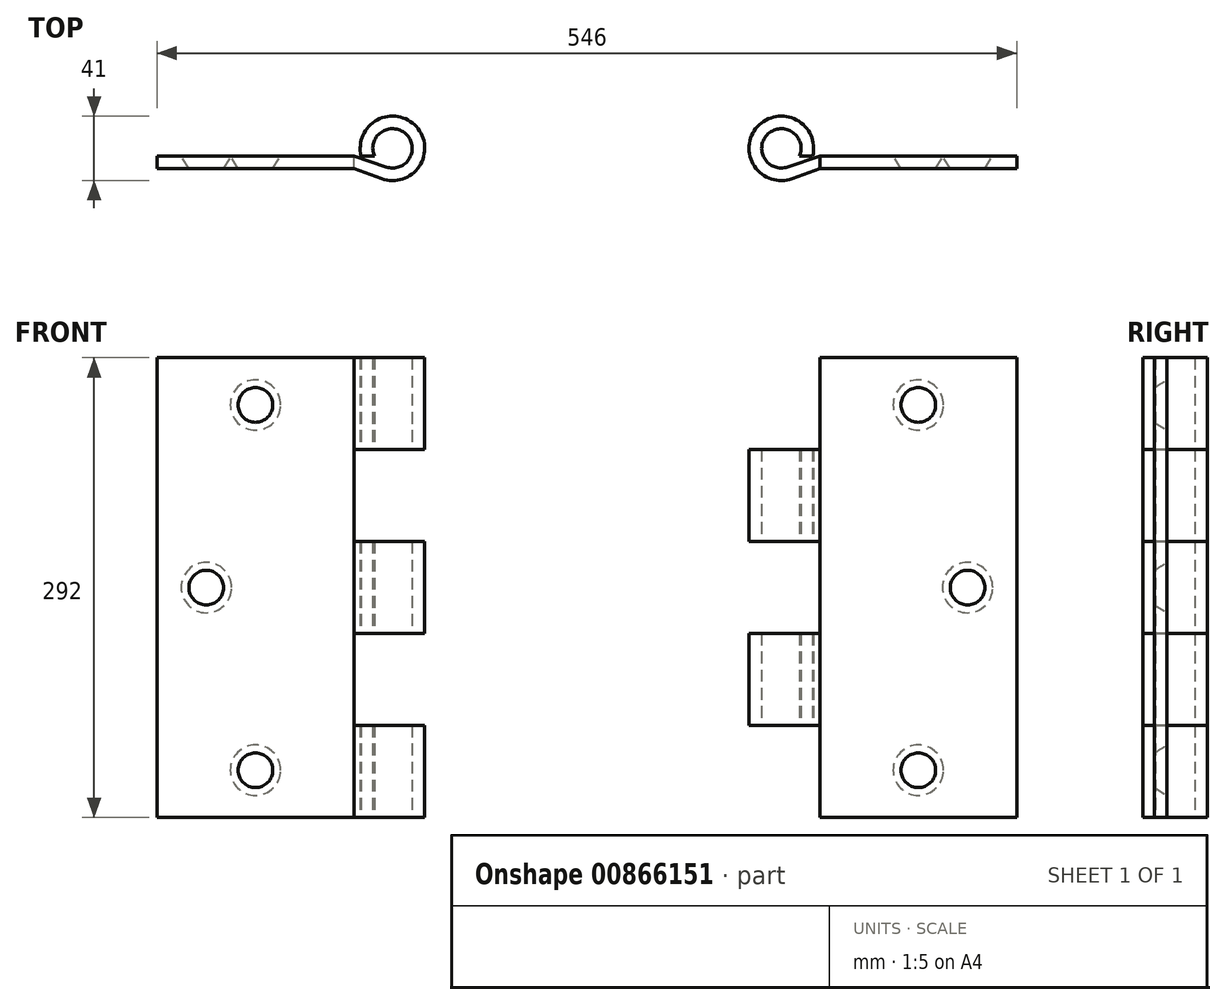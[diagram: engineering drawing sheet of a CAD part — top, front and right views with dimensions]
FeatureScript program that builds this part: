
annotation { "Feature Type Name" : "Feature", "Feature Type Description" : "" }
export const myFeature = defineFeature(function(context is Context, id is Id, definition is map)
    precondition{}
    {
        {
            var Q0;
            Q0=qCreatedBy(makeId("Top.planeOp"),FACE);
            var sketch = newSketch(context, id + "F0", { "sketchPlane" : qUnion([Q0])});
            skLineSegment(sketch, "E0", {"start": v(0, 0) * mm, "end": v(-125, 0) * mm});
            skLineSegment(sketch, "E1", {"start": v(-125, 0) * mm, "end": v(-125, 8) * mm});
            skLineSegment(sketch, "E2", {"start": v(0, 0) * mm, "end": v(0, 0) * mm});
            skLineSegment(sketch, "E3", {"start": v(-125, 8) * mm, "end": v(0, 8) * mm});
            skLineSegment(sketch, "E4", {"start": v(0, 8) * mm, "end": v(0, 13) * mm});
            skArc(sketch, "E5", {"start": v(20.54, 1.14) * mm, "mid": v(32.94, 22.22) * mm, "end": v(13.04, 8) * mm});
            skArc(sketch, "E6", {"start": v(17.59, -6.3) * mm, "mid": v(39.69, 26.77) * mm, "end": v(4.62, 8) * mm});
            skLineSegment(sketch, "E7", {"start": v(0, 0) * mm, "end": v(17.59, -6.3) * mm});
            skLineSegment(sketch, "E8", {"start": v(0, 8) * mm, "end": v(20.54, 1.14) * mm});
            skLineSegment(sketch, "E9", {"start": v(4.62, 8) * mm, "end": v(13.04, 8) * mm});
            skSolve(sketch);
        }
        {
            var Q0;
            Q0=makeQuery(id+"F0.imprint","IMPRINT",FACE,{"disambiguationData":[TD([[makeQuery(id+"F0.imprint","IMPRINT",EDGE,{"derivedFrom":sQuery(id+"F0.wireOp",EDGE,"E0")}),-1.0]])]});
            extrude(context, id + "F1", {"entities" : qUnion([Q0]), "depth" : 292 * mm, "offsetDistance" : 25 * mm});
        }
        {
            var Q0;
            Q0=makeQuery(id+"F1.opExtrude","SWEPT_FACE",FACE,{"disambiguationData":[OSD([sQuery(id+"F0.wireOp",EDGE,"E3")])]});
            var sketch = newSketch(context, id + "F2", { "sketchPlane" : qUnion([Q0])});
            skLineSegment(sketch, "E10", {"start": v(125, 292) * mm, "end": v(125, 262) * mm});
            skLineSegment(sketch, "E11", {"start": v(125, 292) * mm, "end": v(125, 146) * mm});
            skCircle(sketch, "E12", {"center": v(62.5, 262) * mm, "radius": 16 * mm});
            skPoint(sketch, "E12.centerSnap0", {"position": v(62.5, 292) * mm});
            skCircle(sketch, "E13", {"center": v(93.75, 146) * mm, "radius": 16 * mm});
            skPoint(sketch, "E13.centerSnap0", {"position": v(93.75, 292) * mm});
            skCircle(sketch, "E14", {"center": v(62.5, 30) * mm, "radius": 16 * mm});
            skPoint(sketch, "E15.start.orphan", {"position": v(62.5, 0) * mm});
            skSolve(sketch);
        }
        {
            var Q0;
            Q0=makeQuery(id+"F1.opExtrude","SWEPT_FACE",FACE,{"disambiguationData":[OSD([sQuery(id+"F0.wireOp",EDGE,"E0")])]});
            var sketch = newSketch(context, id + "F3", { "sketchPlane" : qUnion([Q0])});
            skPoint(sketch, "E16.0", {"position": v(-93.75, 146) * mm});
            skPoint(sketch, "E16.1", {"position": v(-62.5, 262) * mm});
            skPoint(sketch, "E16.2", {"position": v(-62.5, 30) * mm});
            skCircle(sketch, "E17", {"center": v(-62.5, 30) * mm, "radius": 11 * mm});
            skCircle(sketch, "E18", {"center": v(-93.75, 146) * mm, "radius": 11 * mm});
            skCircle(sketch, "E19", {"center": v(-62.5, 262) * mm, "radius": 11 * mm});
            skSolve(sketch);
        }
        {
            var Q1;
            Q1=makeQuery(id+"F2.imprint","IMPRINT",FACE,{"disambiguationData":[TD([[makeQuery(id+"F2.imprint","IMPRINT",EDGE,{"derivedFrom":sQuery(id+"F2.wireOp",EDGE,"E14")}),1.0]])]});
            var Q2;
            Q2=makeQuery(id+"F3.imprint","IMPRINT",FACE,{"disambiguationData":[TD([[makeQuery(id+"F3.imprint","IMPRINT",EDGE,{"derivedFrom":sQuery(id+"F3.wireOp",EDGE,"E17")}),1.0]])]});
            loft(context, id + "F4", {"operationType" : NewBodyOperationType.REMOVE, "sheetProfilesArray" : [{ "sheetProfileEntities" : qUnion([Q1]) }, { "sheetProfileEntities" : qUnion([Q2]) }]});
        }
        {
            var Q1;
            Q1=makeQuery(id+"F2.imprint","IMPRINT",FACE,{"disambiguationData":[TD([[makeQuery(id+"F2.imprint","IMPRINT",EDGE,{"derivedFrom":sQuery(id+"F2.wireOp",EDGE,"E13")}),1.0]])]});
            var Q2;
            Q2=makeQuery(id+"F3.imprint","IMPRINT",FACE,{"disambiguationData":[TD([[makeQuery(id+"F3.imprint","IMPRINT",EDGE,{"derivedFrom":sQuery(id+"F3.wireOp",EDGE,"E18")}),1.0]])]});
            loft(context, id + "F5", {"operationType" : NewBodyOperationType.REMOVE, "sheetProfilesArray" : [{ "sheetProfileEntities" : qUnion([Q1]) }, { "sheetProfileEntities" : qUnion([Q2]) }]});
        }
        {
            var Q1;
            Q1=makeQuery(id+"F2.imprint","IMPRINT",FACE,{"disambiguationData":[TD([[makeQuery(id+"F2.imprint","IMPRINT",EDGE,{"derivedFrom":sQuery(id+"F2.wireOp",EDGE,"E12")}),1.0]])]});
            var Q2;
            Q2=makeQuery(id+"F3.imprint","IMPRINT",FACE,{"disambiguationData":[TD([[makeQuery(id+"F3.imprint","IMPRINT",EDGE,{"derivedFrom":sQuery(id+"F3.wireOp",EDGE,"E19")}),1.0]])]});
            loft(context, id + "F6", {"operationType" : NewBodyOperationType.REMOVE, "sheetProfilesArray" : [{ "sheetProfileEntities" : qUnion([Q1]) }, { "sheetProfileEntities" : qUnion([Q2]) }]});
        }
        {
            var Q0;
            Q0=qCreatedBy(makeId("Right.planeOp"),FACE);
            cPlane(context, id + "F7", {"entities" : qUnion([Q0]), "cplaneType" : CPlaneType.OFFSET, "offset" : 148 * mm, "width" : 150 * mm, "height" : 150 * mm});
        }
        {
            var Q0;
            Q0=makeQuery(id+"F1.opExtrude","SWEPT_BODY",BODY,{"disambiguationData":[OSD([sQuery(id+"F0.wireOp",EDGE,"E0"),sQuery(id+"F0.wireOp",EDGE,"E1"),sQuery(id+"F0.wireOp",EDGE,"E3"),sQuery(id+"F0.wireOp",EDGE,"E5"),sQuery(id+"F0.wireOp",EDGE,"E6"),sQuery(id+"F0.wireOp",EDGE,"E7"),sQuery(id+"F0.wireOp",EDGE,"E8"),sQuery(id+"F0.wireOp",EDGE,"E9")])]});
            var Q1;
            Q1=qCreatedBy(id+"F7.planeOp",FACE);
            mirror(context, id + "F8", {"entities" : qUnion([Q0]), "mirrorPlane" : qUnion([Q1])});
        }
        {
            var Q0;
            Q0=makeQuery(id+"F2.imprint","IMPRINT",FACE,{"disambiguationData":[TD([[makeQuery(id+"F2.imprint","IMPRINT",EDGE,{"derivedFrom":sQuery(id+"F2.wireOp",EDGE,"E12")}),-1.0]])]});
            var sketch = newSketch(context, id + "F9", { "sketchPlane" : qUnion([Q0])});
            skLineSegment(sketch, "E20", {"start": v(0, 0) * mm, "end": v(0, 58.4) * mm});
            skLineSegment(sketch, "E21", {"start": v(0, 58.4) * mm, "end": v(-56.85, 58.4) * mm});
            skLineSegment(sketch, "E22", {"start": v(-56.85, 58.4) * mm, "end": v(-56.85, 0) * mm});
            skLineSegment(sketch, "E23", {"start": v(-56.85, 0) * mm, "end": v(0, 0) * mm});
            skLineSegment(sketch, "E24", {"start": v(0, 58.4) * mm, "end": v(0, 116.8) * mm});
            skLineSegment(sketch, "E25", {"start": v(0, 116.8) * mm, "end": v(-63.77, 116.8) * mm});
            skLineSegment(sketch, "E26", {"start": v(-63.77, 116.8) * mm, "end": v(-63.77, 58.4) * mm});
            skLineSegment(sketch, "E27", {"start": v(-63.77, 58.4) * mm, "end": v(-56.85, 58.4) * mm});
            skLineSegment(sketch, "E28", {"start": v(0, 116.8) * mm, "end": v(0, 175.2) * mm});
            skLineSegment(sketch, "E29", {"start": v(0, 175.2) * mm, "end": v(-56.85, 175.2) * mm});
            skLineSegment(sketch, "E30", {"start": v(-56.85, 175.2) * mm, "end": v(-56.85, 116.8) * mm});
            skLineSegment(sketch, "E31", {"start": v(0, 175.2) * mm, "end": v(0, 233.6) * mm});
            skLineSegment(sketch, "E32", {"start": v(0, 233.6) * mm, "end": v(-57.4, 233.6) * mm});
            skLineSegment(sketch, "E33", {"start": v(-57.4, 233.6) * mm, "end": v(-57.4, 175.2) * mm});
            skLineSegment(sketch, "E34", {"start": v(-57.4, 175.2) * mm, "end": v(-56.85, 175.2) * mm});
            skLineSegment(sketch, "E35", {"start": v(0, 233.6) * mm, "end": v(0, 292) * mm});
            skLineSegment(sketch, "E36", {"start": v(0, 292) * mm, "end": v(-69.69, 292) * mm});
            skLineSegment(sketch, "E37", {"start": v(-69.69, 292) * mm, "end": v(-69.69, 233.6) * mm});
            skLineSegment(sketch, "E38", {"start": v(-69.69, 233.6) * mm, "end": v(-57.4, 233.6) * mm});
            skSolve(sketch);
        }
        {
            var Q0;
            Q0=makeQuery(id+"F9.imprint","IMPRINT",FACE,{"disambiguationData":[TD([[makeQuery(id+"F9.imprint","IMPRINT",EDGE,{"derivedFrom":sQuery(id+"F9.wireOp",EDGE,"E29")}),-1.0]])]});
            var Q1;
            Q1=makeQuery(id+"F9.imprint","IMPRINT",FACE,{"disambiguationData":[TD([[makeQuery(id+"F9.imprint","IMPRINT",EDGE,{"derivedFrom":sQuery(id+"F9.wireOp",EDGE,"E21")}),-1.0]])]});
            extrude(context, id + "F10", {"entities" : qUnion([Q0, Q1]), "operationType" : NewBodyOperationType.REMOVE, "endBound" : BoundingType.SYMMETRIC, "oppositeDirection" : true, "depth" : 100 * mm, "offsetDistance" : 25 * mm});
        }
        {
            var Q0;
            Q0=makeQuery(id+"F8.opPattern","COPY",FACE,{"derivedFrom":makeQuery(id+"F1.opExtrude","SWEPT_FACE",FACE,{"disambiguationData":[OSD([sQuery(id+"F0.wireOp",EDGE,"E3")])]}),"instanceName":"1"});
            var sketch = newSketch(context, id + "F11", { "sketchPlane" : qUnion([Q0])});
            skLineSegment(sketch, "E39", {"start": v(-296, 292) * mm, "end": v(-296, 233.6) * mm});
            skLineSegment(sketch, "E40", {"start": v(-296, 233.6) * mm, "end": v(-237.8, 233.6) * mm});
            skLineSegment(sketch, "E41", {"start": v(-237.8, 233.6) * mm, "end": v(-237.8, 175.2) * mm});
            skLineSegment(sketch, "E42", {"start": v(-237.8, 175.2) * mm, "end": v(-296, 175.2) * mm});
            skLineSegment(sketch, "E43", {"start": v(-296, 175.2) * mm, "end": v(-296, 116.8) * mm});
            skLineSegment(sketch, "E44", {"start": v(-296, 116.8) * mm, "end": v(-240.26, 116.8) * mm});
            skLineSegment(sketch, "E45", {"start": v(-240.26, 116.8) * mm, "end": v(-240.26, 58.4) * mm});
            skLineSegment(sketch, "E46", {"start": v(-240.26, 58.4) * mm, "end": v(-296, 58.4) * mm});
            skLineSegment(sketch, "E47", {"start": v(-296, 58.4) * mm, "end": v(-296, 0) * mm});
            skLineSegment(sketch, "E48", {"start": v(-296, 0) * mm, "end": v(-240.3, 0) * mm});
            skLineSegment(sketch, "E49", {"start": v(-240.3, 0) * mm, "end": v(-234.18, 0) * mm});
            skLineSegment(sketch, "E50", {"start": v(-234.18, 0) * mm, "end": v(-234.18, 58.4) * mm});
            skLineSegment(sketch, "E51", {"start": v(-234.18, 58.4) * mm, "end": v(-240.26, 58.4) * mm});
            skLineSegment(sketch, "E52", {"start": v(-296, 58.4) * mm, "end": v(-296, 116.8) * mm});
            skLineSegment(sketch, "E53", {"start": v(-240.26, 116.8) * mm, "end": v(-240.26, 175.2) * mm});
            skLineSegment(sketch, "E54", {"start": v(-237.8, 233.6) * mm, "end": v(-237.8, 292) * mm});
            skLineSegment(sketch, "E55", {"start": v(-237.8, 292) * mm, "end": v(-296, 292) * mm});
            skSolve(sketch);
        }
        {
            var Q0;
            Q0=makeQuery(id+"F11.imprint","IMPRINT",FACE,{"disambiguationData":[TD([[makeQuery(id+"F11.imprint","IMPRINT",EDGE,{"derivedFrom":sQuery(id+"F11.wireOp",EDGE,"E39")}),1.0]])]});
            var Q1;
            {var subQ0=sQuery(id+"F11.wireOp",EDGE,"E43");Q1=makeQuery(id+"F11.imprint","IMPRINT",FACE,{"disambiguationData":[TD([[makeQuery(id+"F11.imprint","IMPRINT",EDGE,{"derivedFrom":subQ0}),1.0]])]});}
            var Q2;
            Q2=makeQuery(id+"F11.imprint","IMPRINT",FACE,{"disambiguationData":[TD([[makeQuery(id+"F11.imprint","IMPRINT",EDGE,{"derivedFrom":sQuery(id+"F11.wireOp",EDGE,"E46")}),1.0]])]});
            extrude(context, id + "F12", {"entities" : qUnion([Q0, Q1, Q2]), "operationType" : NewBodyOperationType.REMOVE, "endBound" : BoundingType.SYMMETRIC, "oppositeDirection" : true, "depth" : 100 * mm, "offsetDistance" : 25 * mm});
        }
    });
